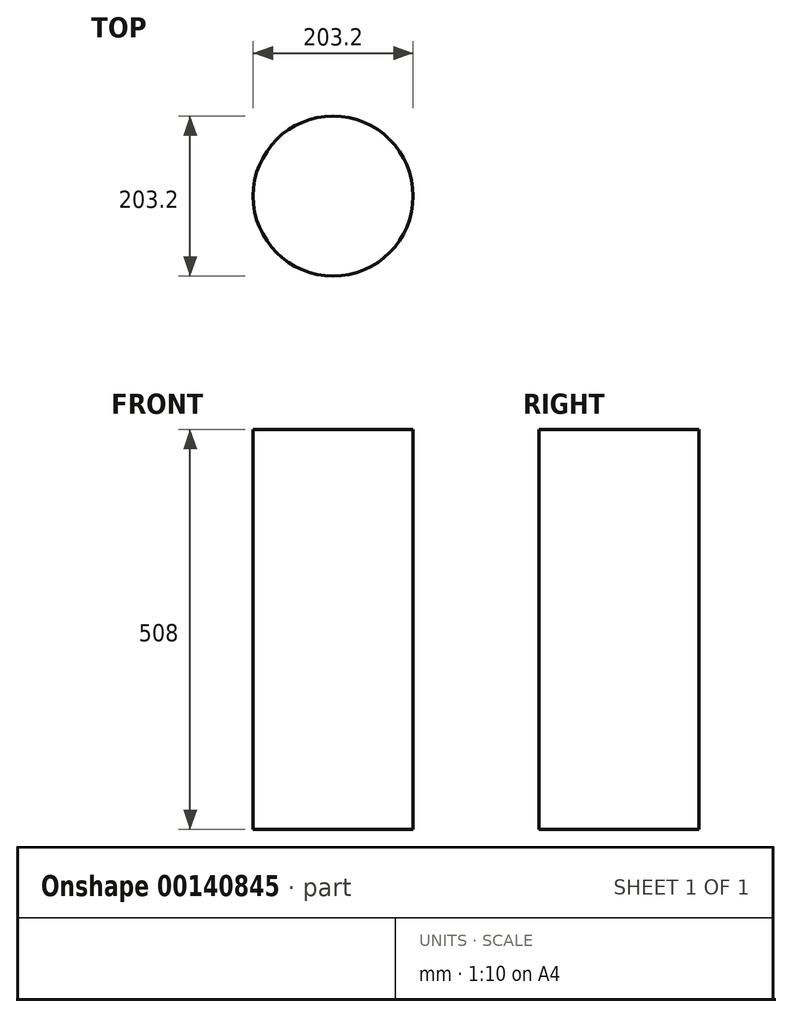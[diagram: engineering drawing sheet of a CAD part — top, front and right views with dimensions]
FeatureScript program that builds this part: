
annotation { "Feature Type Name" : "Feature", "Feature Type Description" : "" }
export const myFeature = defineFeature(function(context is Context, id is Id, definition is map)
    precondition{}
    {
        {
            var Q0;
            Q0=qCreatedBy(makeId("Top.planeOp"),FACE);
            var sketch = newSketch(context, id + "F0", { "sketchPlane" : qUnion([Q0])});
            skCircle(sketch, "E0", {"center": v(0, 0) * mm, "radius": 101.6 * mm});
            skSolve(sketch);
        }
        {
            var Q0;
            Q0=makeQuery(id+"F0.imprint","IMPRINT",FACE,{"disambiguationData":[TD([[makeQuery(id+"F0.imprint","IMPRINT",EDGE,{"derivedFrom":sQuery(id+"F0.wireOp",EDGE,"E0")}),1.0]])]});
            extrude(context, id + "F1", {"entities" : qUnion([Q0]), "depth" : 508 * mm});
        }
    });
